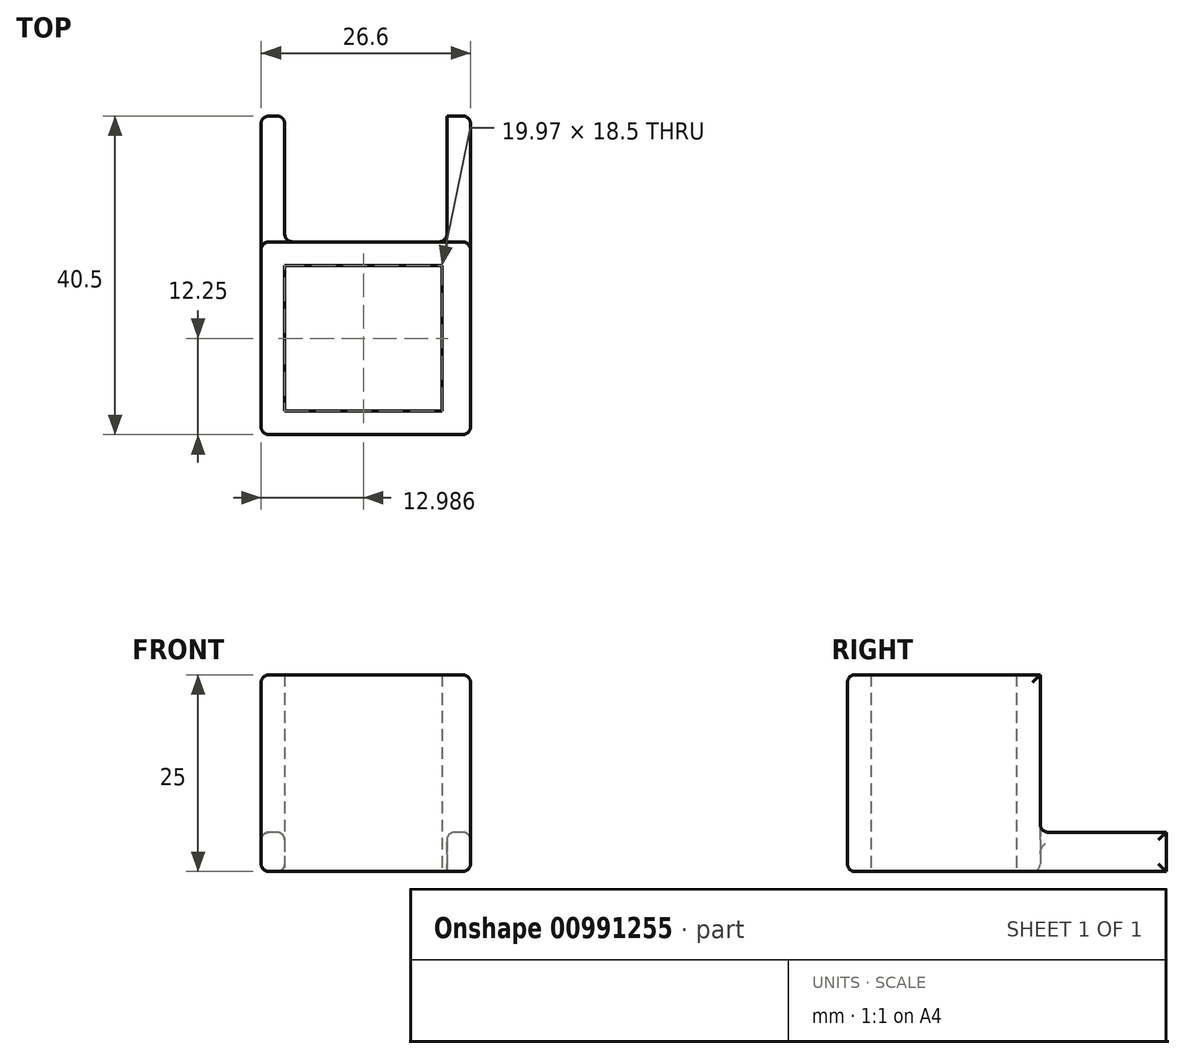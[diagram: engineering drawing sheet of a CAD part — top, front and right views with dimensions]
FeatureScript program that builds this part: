
annotation { "Feature Type Name" : "Feature", "Feature Type Description" : "" }
export const myFeature = defineFeature(function(context is Context, id is Id, definition is map)
    precondition{}
    {
        {
            var Q0;
            Q0=qCreatedBy(makeId("Top.planeOp"),FACE);
            var sketch = newSketch(context, id + "F0", { "sketchPlane" : qUnion([Q0])});
            skLineSegment(sketch, "E0", {"start": v(-13.3, 0) * mm, "end": v(-13.3, 40.5) * mm});
            skLineSegment(sketch, "E1", {"start": v(-13.3, 40.5) * mm, "end": v(-10.3, 40.5) * mm});
            skLineSegment(sketch, "E2", {"start": v(-10.3, 40.5) * mm, "end": v(-10.3, 24.5) * mm});
            skLineSegment(sketch, "E3", {"start": v(-10.3, 24.5) * mm, "end": v(0, 24.5) * mm});
            skLineSegment(sketch, "E4", {"start": v(-13.3, 0) * mm, "end": v(0, 0) * mm});
            skLineSegment(sketch, "E5.MirrorCS", {"start": v(13.3, 0) * mm, "end": v(0, 0) * mm});
            skLineSegment(sketch, "E6.MirrorCS", {"start": v(13.3, 0) * mm, "end": v(13.3, 40.5) * mm});
            skLineSegment(sketch, "E7.MirrorCS", {"start": v(13.3, 40.5) * mm, "end": v(10.3, 40.5) * mm});
            skLineSegment(sketch, "E8.MirrorCS", {"start": v(10.3, 40.5) * mm, "end": v(10.3, 24.5) * mm});
            skLineSegment(sketch, "E9.MirrorCS", {"start": v(10.3, 24.5) * mm, "end": v(0, 24.5) * mm});
            skSolve(sketch);
        }
        {
            var Q0;
            Q0 = qSketchRegion(id + "F0", true);
            extrude(context, id + "F1", {"entities" : qUnion([Q0]), "depth" : 25 * mm, "offsetDistance" : 25 * mm});
        }
        {
            var Q0;
            Q0=makeQuery(id+"F1.opExtrude","SWEPT_FACE",FACE,{"disambiguationData":[OSD([sQuery(id+"F0.wireOp",EDGE,"E0")])]});
            var sketch = newSketch(context, id + "F2", { "sketchPlane" : qUnion([Q0])});
            skLineSegment(sketch, "E10.bottom", {"start": v(-40.5, 5) * mm, "end": v(-24.5, 5) * mm});
            skLineSegment(sketch, "E10.top", {"start": v(-40.5, 25) * mm, "end": v(-24.5, 25) * mm});
            skLineSegment(sketch, "E10.left", {"start": v(-40.5, 5) * mm, "end": v(-40.5, 25) * mm});
            skLineSegment(sketch, "E10.right", {"start": v(-24.5, 5) * mm, "end": v(-24.5, 25) * mm});
            skLineSegment(sketch, "E11", {"start": v(0, 12.5) * mm, "end": v(-40.5, 12.5) * mm, "construction": true});
            skSolve(sketch);
        }
        {
            var Q0;
            Q0 = qSketchRegion(id + "F2", true);
            extrude(context, id + "F3", {"entities" : qUnion([Q0]), "operationType" : NewBodyOperationType.REMOVE, "endBound" : BoundingType.THROUGH_ALL, "oppositeDirection" : true, "depth" : 25 * mm, "offsetDistance" : 25 * mm});
        }
        {
            var Q0;
            Q0=makeQuery(id+"F0.imprint","IMPRINT",FACE,{"disambiguationData":[TD([[makeQuery(id+"F0.imprint","IMPRINT",EDGE,{"derivedFrom":sQuery(id+"F0.wireOp",EDGE,"E0")}),-1.0]])]});
            var sketch = newSketch(context, id + "F4", { "sketchPlane" : qUnion([Q0])});
            skLineSegment(sketch, "E12.bottom", {"start": v(-10.3, 21.5) * mm, "end": v(9.67, 21.5) * mm});
            skLineSegment(sketch, "E12.top", {"start": v(-10.3, 3) * mm, "end": v(9.67, 3) * mm});
            skLineSegment(sketch, "E12.left", {"start": v(-10.3, 21.5) * mm, "end": v(-10.3, 3) * mm});
            skLineSegment(sketch, "E12.right", {"start": v(9.67, 21.5) * mm, "end": v(9.67, 3) * mm});
            skSolve(sketch);
        }
        {
            var Q0;
            Q0 = qSketchRegion(id + "F4", true);
            extrude(context, id + "F5", {"entities" : qUnion([Q0]), "operationType" : NewBodyOperationType.REMOVE, "endBound" : BoundingType.THROUGH_ALL, "depth" : 25 * mm, "offsetDistance" : 25 * mm});
        }
        {
            var Q0;
            Q0=makeQuery(id+"F1.opExtrude","SWEPT_FACE",FACE,{"disambiguationData":[OSD([sQuery(id+"F0.wireOp",EDGE,"E6.MirrorCS")])]});
            var Q1;
            Q1=makeQuery(id+"F1.opExtrude","SWEPT_FACE",FACE,{"disambiguationData":[OSD([sQuery(id+"F0.wireOp",EDGE,"E0")])]});
            var Q2;
            Q2=makeQuery(id+"F1.opExtrude","SWEPT_FACE",FACE,{"disambiguationData":[OSD([sQuery(id+"F0.wireOp",EDGE,"E4"),sQuery(id+"F0.wireOp",EDGE,"E5.MirrorCS")])]});
            var Q3;
            Q3=makeQuery(id+"F3.boolean.opBoolean","MERGE",EDGE,{"derivedFrom":[makeQuery(id+"F1.opExtrude","CAP_EDGE",EDGE,{"disambiguationData":[OSD([sQuery(id+"F0.wireOp",EDGE,"E3"),sQuery(id+"F0.wireOp",EDGE,"E9.MirrorCS")])],"isStart":false})],"fromTools":[makeQuery(id+"F3.opExtrude","SWEPT_EDGE",EDGE,{"disambiguationData":[OSD([sQuery(id+"F0.wireOp",EDGE,"E0"),sQuery(id+"F2.wireOp",EDGE,"E10.top"),sQuery(id+"F2.wireOp",EDGE,"E10.right")])]})]});
            var Q4;
            Q4=makeQuery(id+"F1.opExtrude","CAP_EDGE",EDGE,{"disambiguationData":[OSD([sQuery(id+"F0.wireOp",EDGE,"E3"),sQuery(id+"F0.wireOp",EDGE,"E9.MirrorCS")])],"isStart":true});
            var Q5;
            {var subQ0=sQuery(id+"F2.wireOp",EDGE,"E10.bottom");var subQ1=sQuery(id+"F2.wireOp",EDGE,"E10.right");Q5=makeQuery(id+"F3.boolean.opBoolean","COPY",EDGE,{"disambiguationData":[TD([makeQuery(id+"F1.opExtrude","SWEPT_FACE",FACE,{"disambiguationData":[OSD([sQuery(id+"F0.wireOp",EDGE,"E0")])]})])],"derivedFrom":makeQuery(id+"F3.opExtrude","SWEPT_EDGE",EDGE,{"disambiguationData":[OSD([subQ0,subQ1])]})});}
            var Q6;
            {var subQ0=sQuery(id+"F2.wireOp",EDGE,"E10.bottom");var subQ1=sQuery(id+"F2.wireOp",EDGE,"E10.right");Q6=makeQuery(id+"F3.boolean.opBoolean","COPY",EDGE,{"disambiguationData":[TD([makeQuery(id+"F1.opExtrude","SWEPT_FACE",FACE,{"disambiguationData":[OSD([sQuery(id+"F0.wireOp",EDGE,"E6.MirrorCS")])]})])],"derivedFrom":makeQuery(id+"F3.opExtrude","SWEPT_EDGE",EDGE,{"disambiguationData":[OSD([subQ0,subQ1])]})});}
            var Q7;
            Q7=makeQuery(id+"F3.boolean.opBoolean","INTERSECT",EDGE,{"derivedFrom":[makeQuery(id+"F1.opExtrude","SWEPT_FACE",FACE,{"disambiguationData":[OSD([sQuery(id+"F0.wireOp",EDGE,"E8.MirrorCS")])]}),makeQuery(id+"F3.opExtrude","SWEPT_FACE",FACE,{"disambiguationData":[OSD([sQuery(id+"F2.wireOp",EDGE,"E10.bottom")])]})]});
            var Q8;
            Q8=makeQuery(id+"F1.opExtrude","SWEPT_FACE",FACE,{"disambiguationData":[OSD([sQuery(id+"F0.wireOp",EDGE,"E2")])]});
            fillet(context, id + "F6", {"entities" : qUnion([Q0, Q1, Q2, Q3, Q4, Q5, Q6, Q7, Q8]), "radius" : 1 * mm, "tangentPropagation" : true, "allowEdgeOverflow" : false});
        }
    });
